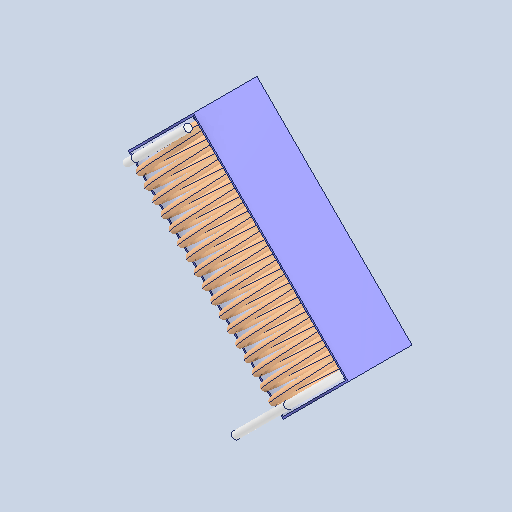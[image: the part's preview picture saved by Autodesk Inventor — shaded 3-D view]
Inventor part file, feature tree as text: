
AUTODESK INVENTOR PART (.ipt)
format: ipt  version: 2025 (Build 290162000, 162)  size: 717,312 bytes
history: native  units: mm
features: sweep x1, other x1
ambient origin geometry x8: Origin, YZ Plane, XZ Plane, XY Plane, X Axis, Y Axis, Z Axis, Center Point
bodies: Solid1 (feature_tree), Solid2 (feature_tree)
feature tree (2):
  sweep  "Sweep9"
  other  "Cut-Extrude1"
